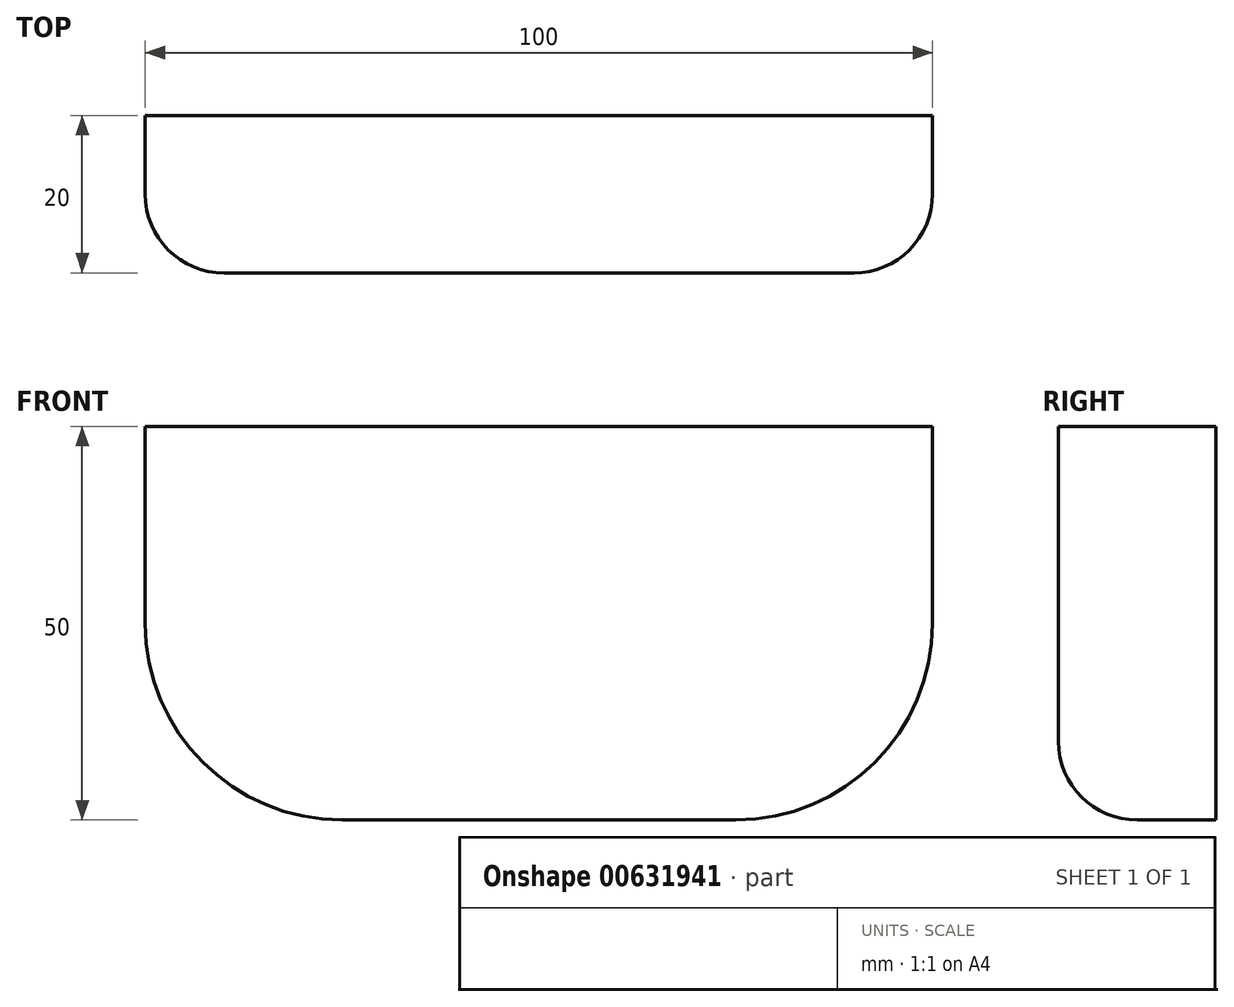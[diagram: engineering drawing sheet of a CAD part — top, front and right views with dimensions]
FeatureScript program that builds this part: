
annotation { "Feature Type Name" : "Feature", "Feature Type Description" : "" }
export const myFeature = defineFeature(function(context is Context, id is Id, definition is map)
    precondition{}
    {
        {
            var Q0;
            Q0=qCreatedBy(makeId("Front.planeOp"),FACE);
            var sketch = newSketch(context, id + "F0", { "sketchPlane" : qUnion([Q0])});
            skLineSegment(sketch, "E0.bottom", {"start": v(-73.16, 80.3) * mm, "end": v(26.84, 80.3) * mm});
            skLineSegment(sketch, "E0.top", {"start": v(-48.16, 30.3) * mm, "end": v(1.84, 30.3) * mm});
            skLineSegment(sketch, "E0.left", {"start": v(-73.16, 80.3) * mm, "end": v(-73.16, 55.3) * mm});
            skLineSegment(sketch, "E0.right", {"start": v(26.84, 80.3) * mm, "end": v(26.84, 55.3) * mm});
            skPoint(sketch, "E1.visualSharp", {"position": v(-73.16, 80.3) * mm});
            skLineSegment(sketch, "E1.filletArc", {"start": v(-73.16, 80.3) * mm, "end": v(-73.16, 80.3) * mm});
            skPoint(sketch, "E2.visualSharp", {"position": v(26.84, 80.3) * mm});
            skLineSegment(sketch, "E2.filletArc", {"start": v(26.84, 80.3) * mm, "end": v(26.84, 80.3) * mm});
            skPoint(sketch, "E3.visualSharp", {"position": v(26.84, 30.3) * mm});
            skLineSegment(sketch, "E3.filletArc", {"start": v(26.84, 30.3) * mm, "end": v(26.84, 30.3) * mm});
            skPoint(sketch, "E4.visualSharp", {"position": v(-73.16, 30.3) * mm});
            skArc(sketch, "E4.filletArc", {"start": v(-73.16, 55.3) * mm, "mid": v(-65.84, 37.63) * mm, "end": v(-48.16, 30.3) * mm});
            skArc(sketch, "E5.filletArc", {"start": v(1.84, 30.3) * mm, "mid": v(19.52, 37.63) * mm, "end": v(26.84, 55.3) * mm});
            skSolve(sketch);
        }
        {
            var Q0;
            Q0=makeQuery(id+"F0.imprint","IMPRINT",FACE,{"disambiguationData":[TD([[makeQuery(id+"F0.imprint","IMPRINT",EDGE,{"derivedFrom":sQuery(id+"F0.wireOp",EDGE,"E0.bottom")}),-1.0]])]});
            extrude(context, id + "F1", {"entities" : qUnion([Q0]), "depth" : 20 * mm, "offsetDistance" : 25 * mm});
        }
        {
            var Q0;
            Q0=makeQuery(id+"F1.opExtrude","CAP_EDGE",EDGE,{"disambiguationData":[OSD([sQuery(id+"F0.wireOp",EDGE,"E0.left")])],"isStart":false});
            fillet(context, id + "F2", {"entities" : qUnion([Q0]), "radius" : 10 * mm, "tangentPropagation" : true, "allowEdgeOverflow" : false});
        }
    });
